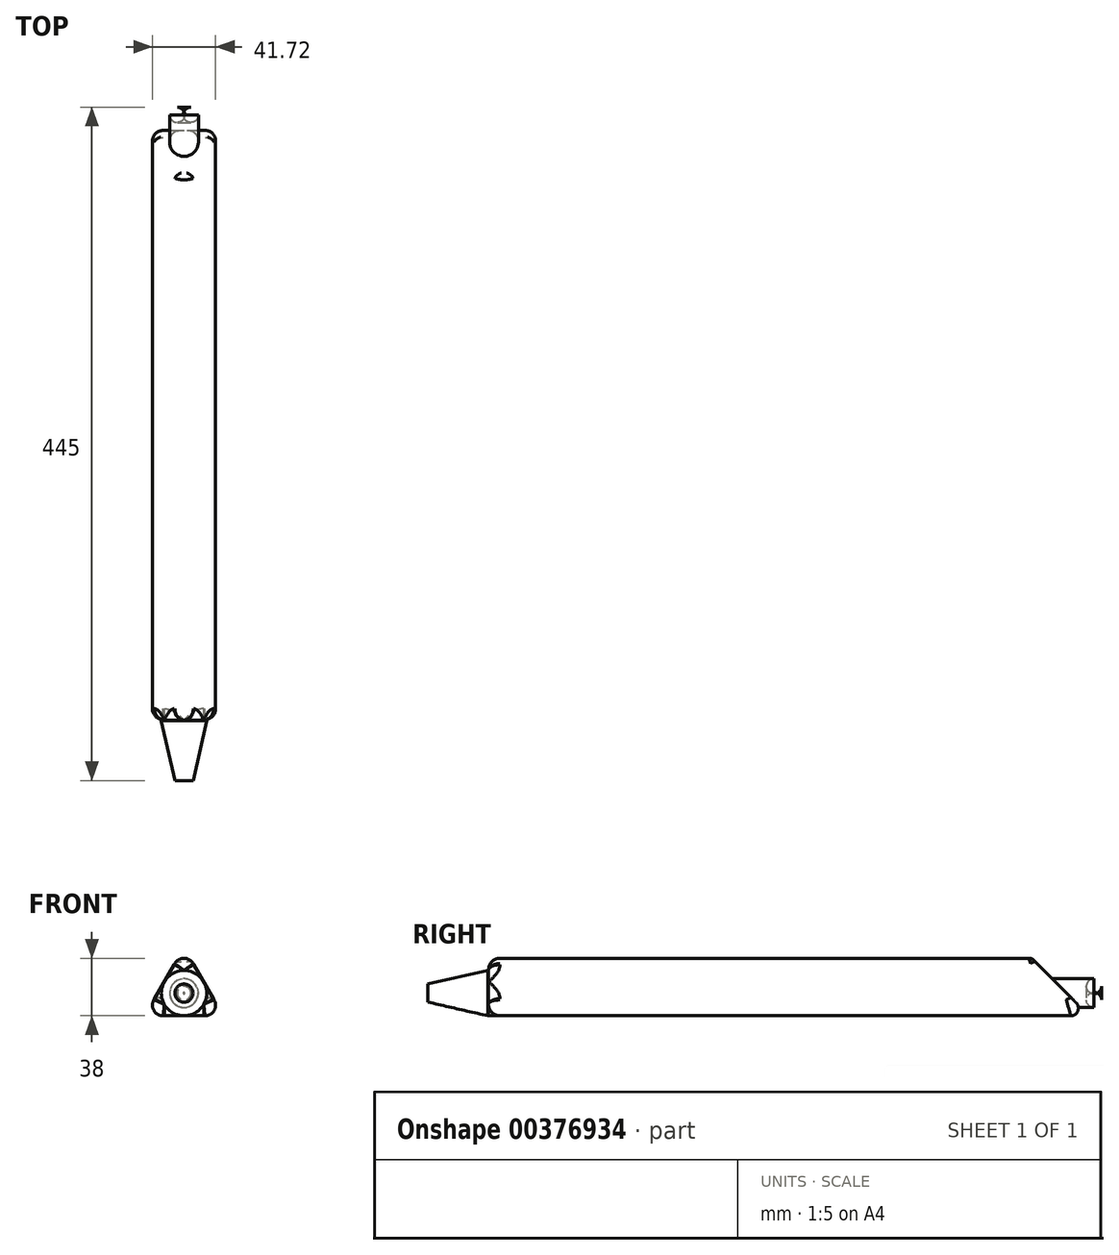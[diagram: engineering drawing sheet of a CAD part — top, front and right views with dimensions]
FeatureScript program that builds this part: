
annotation { "Feature Type Name" : "Feature", "Feature Type Description" : "" }
export const myFeature = defineFeature(function(context is Context, id is Id, definition is map)
    precondition{}
    {
        {
            var Q0;
            Q0=qCreatedBy(makeId("Front.planeOp"),FACE);
            var sketch = newSketch(context, id + "F0", { "sketchPlane" : qUnion([Q0])});
            skCircle(sketch, "E0.cCircle", {"center": v(0, 0) * mm, "radius": 15 * mm, "construction": true});
            skLineSegment(sketch, "E0.0", {"start": v(0, 30) * mm, "end": v(25.98, -15) * mm});
            skLineSegment(sketch, "E0.1", {"start": v(25.98, -15) * mm, "end": v(-25.98, -15) * mm});
            skLineSegment(sketch, "E0.2", {"start": v(-25.98, -15) * mm, "end": v(0, 30) * mm});
            skPoint(sketch, "E0.0.midPoint", {"position": v(13, 7.5) * mm});
            skLineSegment(sketch, "E1.bottom", {"start": v(-13.44, -44.79) * mm, "end": v(11.76, -44.79) * mm});
            skLineSegment(sketch, "E1.top", {"start": v(-13.44, -54.5) * mm, "end": v(11.76, -54.5) * mm});
            skLineSegment(sketch, "E1.left", {"start": v(-13.44, -44.79) * mm, "end": v(-13.44, -54.5) * mm});
            skLineSegment(sketch, "E1.right", {"start": v(11.76, -44.79) * mm, "end": v(11.76, -54.5) * mm});
            skSolve(sketch);
        }
        {
            var Q0;
            Q0=makeQuery(id+"F0.imprint","IMPRINT",FACE,{"disambiguationData":[TD([[makeQuery(id+"F0.imprint","IMPRINT",EDGE,{"derivedFrom":sQuery(id+"F0.wireOp",EDGE,"E0.0")}),-1.0]])]});
            extrude(context, id + "F1", {"entities" : qUnion([Q0]), "depth" : 400 * mm});
        }
        {
            var Q0;
            Q0=qCreatedBy(makeId("Right.planeOp"),FACE);
            var sketch = newSketch(context, id + "F2", { "sketchPlane" : qUnion([Q0])});
            skLineSegment(sketch, "E2", {"start": v(0, -18.38) * mm, "end": v(0, 39.65) * mm});
            skLineSegment(sketch, "E3", {"start": v(0, 39.65) * mm, "end": v(-57.22, 39.65) * mm});
            skLineSegment(sketch, "E4", {"start": v(-57.22, 39.65) * mm, "end": v(0, -18.38) * mm});
            skSolve(sketch);
        }
        {
            var Q0;
            Q0=makeQuery(id+"F2.imprint","IMPRINT",FACE,{"disambiguationData":[TD([[makeQuery(id+"F2.imprint","IMPRINT",EDGE,{"derivedFrom":sQuery(id+"F2.wireOp",EDGE,"E2")}),1.0]])]});
            extrude(context, id + "F3", {"entities" : qUnion([Q0]), "operationType" : NewBodyOperationType.REMOVE, "endBound" : BoundingType.SYMMETRIC, "oppositeDirection" : true, "depth" : 60 * mm});
        }
        {
            var Q0;
            Q0=makeQuery(id+"F1.opExtrude","SWEPT_EDGE",EDGE,{"disambiguationData":[OSD([sQuery(id+"F0.wireOp",EDGE,"E0.0"),sQuery(id+"F0.wireOp",EDGE,"E0.2")])]});
            var Q1;
            Q1=makeQuery(id+"F1.opExtrude","SWEPT_EDGE",EDGE,{"disambiguationData":[OSD([sQuery(id+"F0.wireOp",EDGE,"E0.0"),sQuery(id+"F0.wireOp",EDGE,"E0.1")])]});
            var Q2;
            Q2=makeQuery(id+"F1.opExtrude","SWEPT_EDGE",EDGE,{"disambiguationData":[OSD([sQuery(id+"F0.wireOp",EDGE,"E0.1"),sQuery(id+"F0.wireOp",EDGE,"E0.2")])]});
            fillet(context, id + "F4", {"entities" : qUnion([Q0, Q1, Q2]), "radius" : 7 * mm, "tangentPropagation" : true, "allowEdgeOverflow" : false});
        }
        {
            var Q0;
            Q0=makeQuery(id+"F1.opExtrude","CAP_FACE",FACE,{"disambiguationData":[OSD([sQuery(id+"F0.wireOp",EDGE,"E0.0"),sQuery(id+"F0.wireOp",EDGE,"E0.1"),sQuery(id+"F0.wireOp",EDGE,"E0.2")])],"isStart":false});
            var sketch = newSketch(context, id + "F5", { "sketchPlane" : qUnion([Q0])});
            skCircle(sketch, "E5", {"center": v(0, 0) * mm, "radius": 15 * mm});
            skSolve(sketch);
        }
        {
            var Q0;
            {var subQ0=sQuery(id+"F5.wireOp",EDGE,"E5");var subQ1=makeQuery(id+"F5.imprint","INTERSECT",VERTEX,{"derivedFrom":[makeQuery(id+"F1.opExtrude","CAP_EDGE",EDGE,{"disambiguationData":[OSD([sQuery(id+"F0.wireOp",EDGE,"E0.2")])],"isStart":false}),subQ0]});Q0=makeQuery(id+"F5.imprint","IMPRINT",FACE,{"disambiguationData":[TD([[makeQuery(id+"F5.imprint","IMPRINT",EDGE,{"disambiguationData":[TD([[subQ1,1.0]])],"derivedFrom":subQ0}),1.0]])]});}
            extrude(context, id + "F6", {"entities" : qUnion([Q0]), "operationType" : NewBodyOperationType.ADD, "depth" : 40 * mm});
        }
        {
            var Q0;
            Q0=makeQuery(id+"F6.opExtrude","CAP_EDGE",EDGE,{"disambiguationData":[OSD([sQuery(id+"F5.wireOp",EDGE,"E5")])],"isStart":false});
            chamfer(context, id + "F7", {"entities" : qUnion([Q0]), "chamferType" : ChamferType.OFFSET_ANGLE, "width" : 9 * mm, "oppositeDirection" : false, "angle" : 77.2 * degree, "tangentPropagation" : true});
        }
        {
            var Q0;
            {var subQ0=sQuery(id+"F0.wireOp",EDGE,"E0.2");var subQ1=sQuery(id+"F0.wireOp",EDGE,"E0.0");Q0=makeQuery(id+"F4.opFillet","BLEND_EDGE",EDGE,{"blendedFrom":[makeQuery(id+"F1.opExtrude","SWEPT_EDGE",EDGE,{"disambiguationData":[OSD([subQ1,subQ0])]}),makeQuery(id+"F1.opExtrude","CAP_FACE",FACE,{"disambiguationData":[OSD([subQ1,sQuery(id+"F0.wireOp",EDGE,"E0.1"),subQ0])],"isStart":false})],"blendedInto":[makeQuery(id+"F1.opExtrude","CAP_FACE",FACE,{"disambiguationData":[OSD([subQ1,sQuery(id+"F0.wireOp",EDGE,"E0.1"),subQ0])],"isStart":false})]});}
            fillet(context, id + "F8", {"entities" : qUnion([Q0]), "radius" : 7.5 * mm, "tangentPropagation" : true, "allowEdgeOverflow" : false});
        }
        {
            var Q0;
            Q0=makeQuery(id+"F3.boolean.opBoolean","COPY",FACE,{"derivedFrom":makeQuery(id+"F3.opExtrude","SWEPT_FACE",FACE,{"disambiguationData":[OSD([sQuery(id+"F2.wireOp",EDGE,"E4")])]})});
            fillet(context, id + "F9", {"entities" : qUnion([Q0]), "radius" : 5 * mm, "tangentPropagation" : true, "allowEdgeOverflow" : false});
        }
        {
            var Q0;
            Q0=qCreatedBy(makeId("Front.planeOp"),FACE);
            var sketch = newSketch(context, id + "F10", { "sketchPlane" : qUnion([Q0])});
            skCircle(sketch, "E6", {"center": v(0, 0) * mm, "radius": 9.5 * mm});
            skSolve(sketch);
        }
        {
            var Q0;
            Q0=makeQuery(id+"F10.imprint","IMPRINT",FACE,{"disambiguationData":[TD([[makeQuery(id+"F10.imprint","IMPRINT",EDGE,{"derivedFrom":sQuery(id+"F10.wireOp",EDGE,"E6")}),1.0]])]});
            extrude(context, id + "F11", {"entities" : qUnion([Q0]), "operationType" : NewBodyOperationType.ADD, "depth" : 30 * mm});
        }
        {
            var Q0;
            Q0=makeQuery(id+"F11.opExtrude","CAP_FACE",FACE,{"disambiguationData":[OSD([sQuery(id+"F10.wireOp",EDGE,"E6")])],"isStart":true});
            extrude(context, id + "F12", {"entities" : qUnion([Q0]), "operationType" : NewBodyOperationType.ADD, "depth" : 5 * mm});
        }
        {
            var Q0;
            Q0=makeQuery(id+"F12.opExtrude","CAP_EDGE",EDGE,{"disambiguationData":[OSD([sQuery(id+"F10.wireOp",EDGE,"E6")])],"isStart":false});
            fillet(context, id + "F13", {"entities" : qUnion([Q0]), "radius" : 5 * mm, "tangentPropagation" : true, "allowEdgeOverflow" : false});
        }
    });
